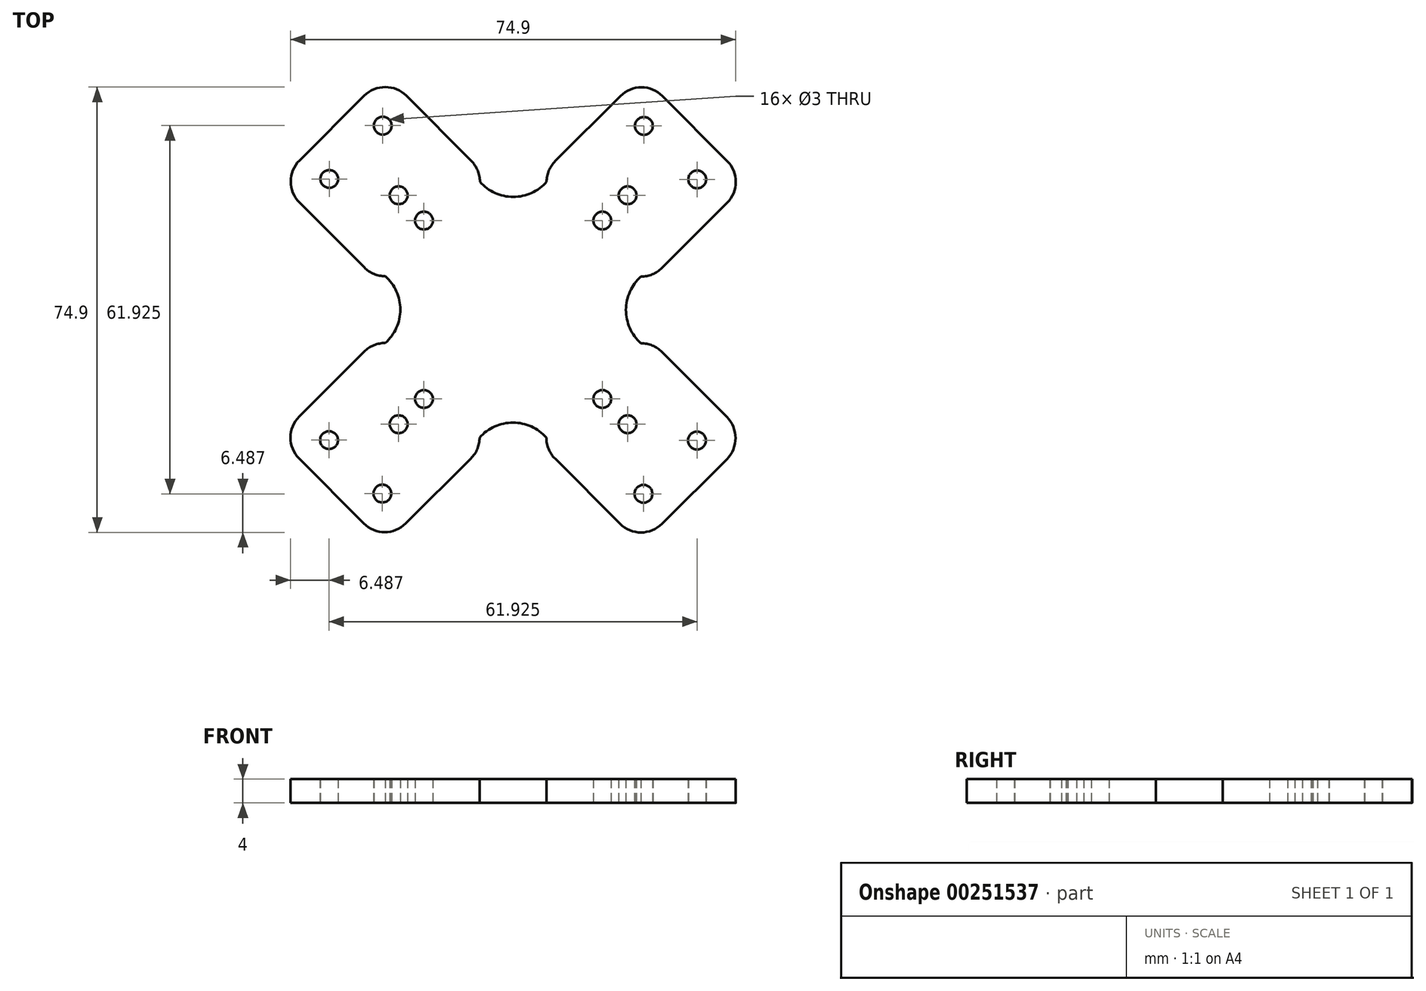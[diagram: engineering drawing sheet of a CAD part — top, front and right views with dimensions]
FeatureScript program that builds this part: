
annotation { "Feature Type Name" : "Feature", "Feature Type Description" : "" }
export const myFeature = defineFeature(function(context is Context, id is Id, definition is map)
    precondition{}
    {
        {
            var Q0;
            Q0=qCreatedBy(makeId("Top.planeOp"),FACE);
            var sketch = newSketch(context, id + "F0", { "sketchPlane" : qUnion([Q0])});
            skPoint(sketch, "E0.middle", {"position": v(0, 0) * mm});
            skCircle(sketch, "E1", {"center": v(-19.25, 19.25) * mm, "radius": 1.5 * mm});
            skCircle(sketch, "E2", {"center": v(19.25, 19.25) * mm, "radius": 1.5 * mm});
            skCircle(sketch, "E3", {"center": v(19.25, -19.25) * mm, "radius": 1.5 * mm});
            skCircle(sketch, "E4", {"center": v(-19.25, -19.25) * mm, "radius": 1.5 * mm});
            skLineSegment(sketch, "E5.top", {"start": v(-3.56, -21.5) * mm, "end": v(-5.64, -21.5) * mm, "construction": true});
            skLineSegment(sketch, "E5.right", {"start": v(-21.5, -3.51) * mm, "end": v(-21.5, -5.59) * mm, "construction": true});
            skLineSegment(sketch, "E6", {"start": v(-25.04, -7.05) * mm, "end": v(-35.99, -17.96) * mm});
            skLineSegment(sketch, "E7", {"start": v(-7.1, -25.03) * mm, "end": v(-18.05, -35.94) * mm});
            skLineSegment(sketch, "E8", {"start": v(-36, -25.03) * mm, "end": v(-25.12, -35.94) * mm});
            skPoint(sketch, "E9.visualSharp", {"position": v(-39.53, -21.5) * mm});
            skArc(sketch, "E9.filletArc", {"start": v(-35.99, -17.96) * mm, "mid": v(-37.45, -21.5) * mm, "end": v(-36, -25.03) * mm});
            skPoint(sketch, "E10.visualSharp", {"position": v(-21.59, -39.47) * mm});
            skArc(sketch, "E10.filletArc", {"start": v(-25.12, -35.94) * mm, "mid": v(-21.58, -37.4) * mm, "end": v(-18.05, -35.94) * mm});
            skPoint(sketch, "E11.visualSharp", {"position": v(-21.5, -3.51) * mm});
            skArc(sketch, "E11.filletArc", {"start": v(-21.5, -5.59) * mm, "mid": v(-23.42, -5.96) * mm, "end": v(-25.04, -7.05) * mm});
            skPoint(sketch, "E12.visualSharp", {"position": v(-3.56, -21.5) * mm});
            skArc(sketch, "E12.filletArc", {"start": v(-7.1, -25.03) * mm, "mid": v(-6.02, -23.4) * mm, "end": v(-5.64, -21.5) * mm});
            skLineSegment(sketch, "E13", {"start": v(-21.53, -21.47) * mm, "end": v(-26.47, -26.42) * mm, "construction": true});
            skArc(sketch, "E14.1.0", {"start": v(5.59, -21.5) * mm, "mid": v(5.96, -23.42) * mm, "end": v(7.05, -25.04) * mm});
            skLineSegment(sketch, "E14.1.1", {"start": v(7.05, -25.04) * mm, "end": v(17.96, -35.99) * mm});
            skArc(sketch, "E14.1.2", {"start": v(17.96, -35.99) * mm, "mid": v(21.5, -37.45) * mm, "end": v(25.03, -36) * mm});
            skLineSegment(sketch, "E14.1.3", {"start": v(25.03, -36) * mm, "end": v(35.94, -25.12) * mm});
            skArc(sketch, "E14.1.4", {"start": v(35.94, -25.12) * mm, "mid": v(37.4, -21.58) * mm, "end": v(35.94, -18.05) * mm});
            skLineSegment(sketch, "E14.1.5", {"start": v(25.03, -7.1) * mm, "end": v(35.94, -18.05) * mm});
            skArc(sketch, "E14.1.6", {"start": v(25.03, -7.1) * mm, "mid": v(23.4, -6.02) * mm, "end": v(21.5, -5.64) * mm});
            skLineSegment(sketch, "E14.1.8", {"start": v(21.47, -21.53) * mm, "end": v(26.42, -26.47) * mm, "construction": true});
            skArc(sketch, "E14.2.0", {"start": v(21.5, 5.59) * mm, "mid": v(23.42, 5.96) * mm, "end": v(25.04, 7.05) * mm});
            skLineSegment(sketch, "E14.2.1", {"start": v(25.04, 7.05) * mm, "end": v(35.99, 17.96) * mm});
            skArc(sketch, "E14.2.2", {"start": v(35.99, 17.96) * mm, "mid": v(37.45, 21.5) * mm, "end": v(36, 25.03) * mm});
            skLineSegment(sketch, "E14.2.3", {"start": v(36, 25.03) * mm, "end": v(25.12, 35.94) * mm});
            skArc(sketch, "E14.2.4", {"start": v(25.12, 35.94) * mm, "mid": v(21.58, 37.4) * mm, "end": v(18.05, 35.94) * mm});
            skLineSegment(sketch, "E14.2.5", {"start": v(7.1, 25.03) * mm, "end": v(18.05, 35.94) * mm});
            skArc(sketch, "E14.2.6", {"start": v(7.1, 25.03) * mm, "mid": v(6.02, 23.42) * mm, "end": v(5.64, 21.51) * mm});
            skLineSegment(sketch, "E14.2.8", {"start": v(21.53, 21.47) * mm, "end": v(26.47, 26.42) * mm, "construction": true});
            skArc(sketch, "E14.3.0", {"start": v(-5.59, 21.51) * mm, "mid": v(-5.96, 23.42) * mm, "end": v(-7.05, 25.04) * mm});
            skLineSegment(sketch, "E14.3.1", {"start": v(-7.05, 25.04) * mm, "end": v(-17.96, 35.99) * mm});
            skArc(sketch, "E14.3.2", {"start": v(-17.96, 35.99) * mm, "mid": v(-21.5, 37.45) * mm, "end": v(-25.03, 36) * mm});
            skLineSegment(sketch, "E14.3.3", {"start": v(-25.03, 36) * mm, "end": v(-35.94, 25.12) * mm});
            skArc(sketch, "E14.3.4", {"start": v(-35.94, 25.12) * mm, "mid": v(-37.4, 21.58) * mm, "end": v(-35.94, 18.05) * mm});
            skLineSegment(sketch, "E14.3.5", {"start": v(-25.03, 7.1) * mm, "end": v(-35.94, 18.05) * mm});
            skArc(sketch, "E14.3.6", {"start": v(-25.03, 7.1) * mm, "mid": v(-23.4, 6.02) * mm, "end": v(-21.5, 5.64) * mm});
            skLineSegment(sketch, "E14.3.8", {"start": v(-21.47, 21.53) * mm, "end": v(-26.42, 26.47) * mm, "construction": true});
            skLineSegment(sketch, "E15.bottom", {"start": v(15, 15) * mm, "end": v(-15, 15) * mm, "construction": true});
            skLineSegment(sketch, "E15.top", {"start": v(15, -15) * mm, "end": v(-15, -15) * mm, "construction": true});
            skLineSegment(sketch, "E15.left", {"start": v(15, 15) * mm, "end": v(15, -15) * mm, "construction": true});
            skLineSegment(sketch, "E15.right", {"start": v(-15, 15) * mm, "end": v(-15, -15) * mm, "construction": true});
            skCircle(sketch, "E16", {"center": v(-15, 15) * mm, "radius": 1.5 * mm});
            skCircle(sketch, "E17", {"center": v(15, 15) * mm, "radius": 1.5 * mm});
            skCircle(sketch, "E18", {"center": v(15, -15) * mm, "radius": 1.5 * mm});
            skCircle(sketch, "E19", {"center": v(-15, -15) * mm, "radius": 1.5 * mm});
            skPoint(sketch, "E20.orphan", {"position": v(-21.47, 21.53) * mm});
            skPoint(sketch, "E21.orphan", {"position": v(21.53, 21.47) * mm});
            skPoint(sketch, "E22.orphan", {"position": v(21.47, -21.53) * mm});
            skArc(sketch, "E23", {"start": v(-21.5, -5.59) * mm, "mid": v(-18.98, 0.02) * mm, "end": v(-21.5, 5.64) * mm});
            skArc(sketch, "E24", {"start": v(-5.59, 21.51) * mm, "mid": v(0.03, 18.99) * mm, "end": v(5.64, 21.51) * mm});
            skArc(sketch, "E25", {"start": v(21.5, 5.59) * mm, "mid": v(18.98, -0.02) * mm, "end": v(21.5, -5.64) * mm});
            skArc(sketch, "E26", {"start": v(5.59, -21.5) * mm, "mid": v(-0.02, -18.98) * mm, "end": v(-5.64, -21.5) * mm});
            skLineSegment(sketch, "E27", {"start": v(-26.47, -26.42) * mm, "end": v(-35.45, -17.43) * mm, "construction": true});
            skCircle(sketch, "E28", {"center": v(-30.96, -21.93) * mm, "radius": 1.5 * mm});
            skLineSegment(sketch, "E29", {"start": v(-26.47, -26.42) * mm, "end": v(-17.51, -35.4) * mm, "construction": true});
            skCircle(sketch, "E30", {"center": v(-22, -30.92) * mm, "radius": 1.5 * mm});
            skCircle(sketch, "E31.1.0", {"center": v(21.93, -30.96) * mm, "radius": 1.5 * mm});
            skCircle(sketch, "E31.1.1", {"center": v(30.92, -22) * mm, "radius": 1.5 * mm});
            skLineSegment(sketch, "E31.1.2", {"start": v(26.42, -26.47) * mm, "end": v(35.4, -17.51) * mm, "construction": true});
            skLineSegment(sketch, "E31.1.3", {"start": v(26.42, -26.47) * mm, "end": v(17.43, -35.45) * mm, "construction": true});
            skCircle(sketch, "E31.2.0", {"center": v(30.96, 21.93) * mm, "radius": 1.5 * mm});
            skCircle(sketch, "E31.2.1", {"center": v(22, 30.92) * mm, "radius": 1.5 * mm});
            skLineSegment(sketch, "E31.2.2", {"start": v(26.47, 26.42) * mm, "end": v(17.51, 35.4) * mm, "construction": true});
            skLineSegment(sketch, "E31.2.3", {"start": v(26.47, 26.42) * mm, "end": v(35.45, 17.43) * mm, "construction": true});
            skCircle(sketch, "E31.3.0", {"center": v(-21.93, 30.96) * mm, "radius": 1.5 * mm});
            skCircle(sketch, "E31.3.1", {"center": v(-30.92, 22) * mm, "radius": 1.5 * mm});
            skLineSegment(sketch, "E31.3.2", {"start": v(-26.42, 26.47) * mm, "end": v(-35.4, 17.51) * mm, "construction": true});
            skLineSegment(sketch, "E31.3.3", {"start": v(-26.42, 26.47) * mm, "end": v(-17.43, 35.45) * mm, "construction": true});
            skLineSegment(sketch, "E32", {"start": v(19.25, 19.25) * mm, "end": v(67.59, 67.08) * mm, "construction": true});
            skLineSegment(sketch, "E33", {"start": v(-19.25, -19.25) * mm, "end": v(-67.39, -67.28) * mm, "construction": true});
            skLineSegment(sketch, "E34", {"start": v(-19.25, 19.25) * mm, "end": v(-30.46, 30.58) * mm, "construction": true});
            skLineSegment(sketch, "E35", {"start": v(19.25, -19.25) * mm, "end": v(67.3, -67.37) * mm, "construction": true});
            skSolve(sketch);
        }
        {
            var Q0;
            Q0=makeQuery(id+"F0.imprint","IMPRINT",FACE,{"disambiguationData":[TD([[makeQuery(id+"F0.imprint","IMPRINT",EDGE,{"derivedFrom":sQuery(id+"F0.wireOp",EDGE,"E1")}),-1.0]])]});
            extrude(context, id + "F1", {"entities" : qUnion([Q0]), "depth" : 4 * mm});
        }
    });
